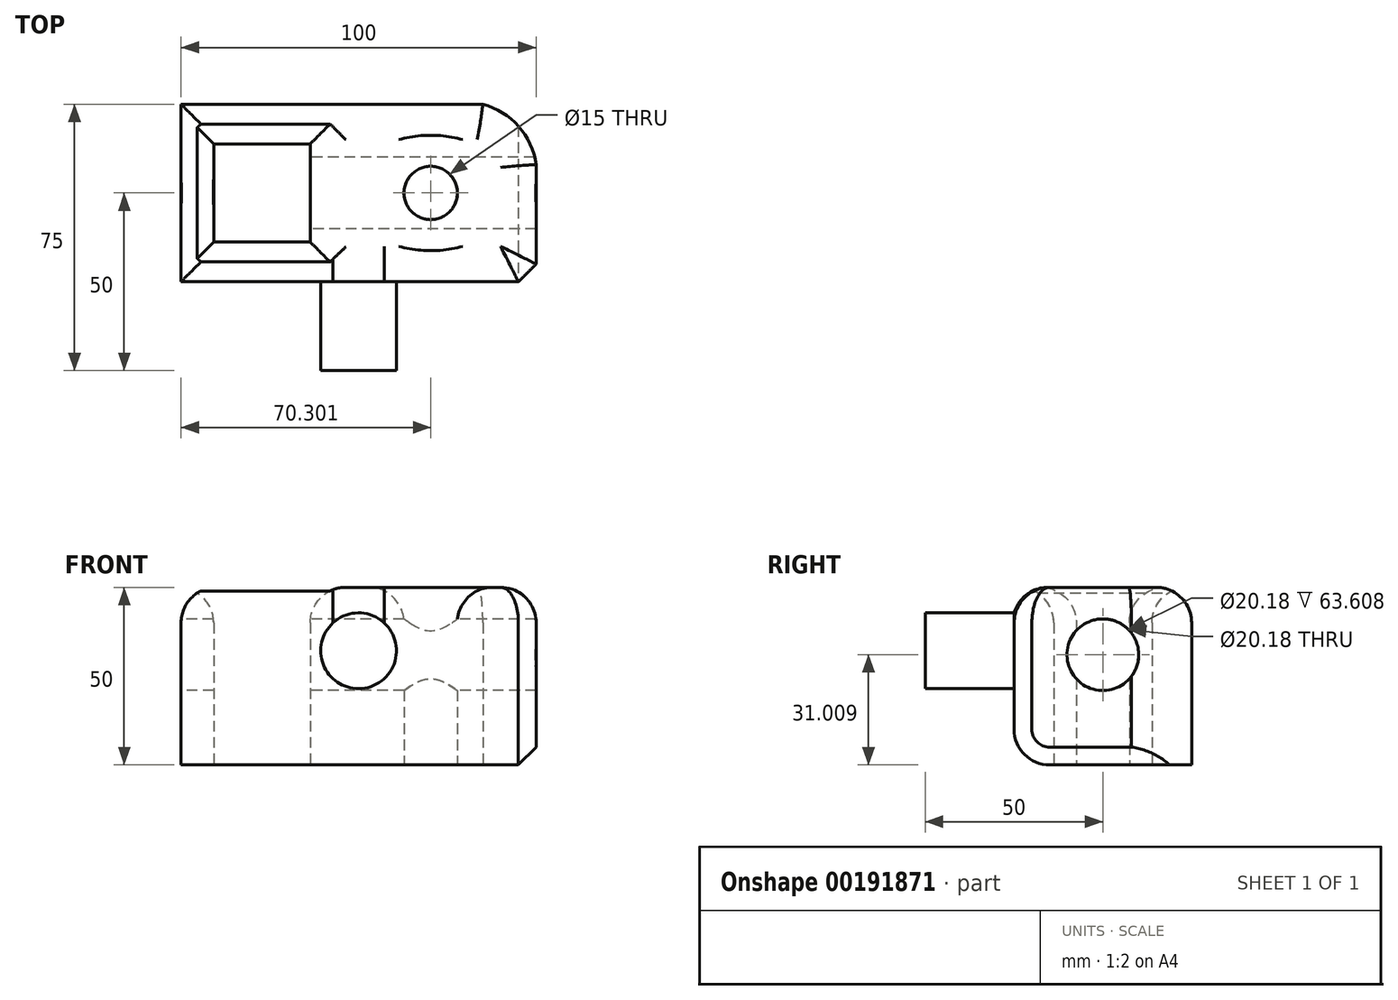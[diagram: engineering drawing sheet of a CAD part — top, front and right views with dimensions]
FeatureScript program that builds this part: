
annotation { "Feature Type Name" : "Feature", "Feature Type Description" : "" }
export const myFeature = defineFeature(function(context is Context, id is Id, definition is map)
    precondition{}
    {
        {
            var Q0;
            Q0=qCreatedBy(makeId("Top.planeOp"),FACE);
            var sketch = newSketch(context, id + "F0", { "sketchPlane" : qUnion([Q0])});
            skLineSegment(sketch, "E0.bottom", {"start": v(50, -25) * mm, "end": v(-50, -25) * mm});
            skLineSegment(sketch, "E0.top", {"start": v(35, 25) * mm, "end": v(-50, 25) * mm});
            skLineSegment(sketch, "E0.left", {"start": v(50, -25) * mm, "end": v(50, 8.03) * mm});
            skLineSegment(sketch, "E0.right", {"start": v(-50, -25) * mm, "end": v(-50, 25) * mm});
            skPoint(sketch, "E0.middle", {"position": v(0, 0) * mm});
            skLineSegment(sketch, "E1.bottom", {"start": v(-13.6, -13.83) * mm, "end": v(-40.83, -13.83) * mm});
            skLineSegment(sketch, "E1.top", {"start": v(-13.6, 13.83) * mm, "end": v(-40.83, 13.83) * mm});
            skLineSegment(sketch, "E1.left", {"start": v(-13.6, -13.83) * mm, "end": v(-13.6, 13.83) * mm});
            skLineSegment(sketch, "E1.right", {"start": v(-40.83, -13.83) * mm, "end": v(-40.83, 13.83) * mm});
            skPoint(sketch, "E1.middle", {"position": v(-27.22, 0) * mm});
            skPoint(sketch, "E1.middle.positionSnap0", {"position": v(-50, 0) * mm});
            skPoint(sketch, "E1.centerSnap0", {"position": v(-50, 0) * mm});
            skArc(sketch, "E2", {"start": v(50, 8.03) * mm, "mid": v(45.05, 18.77) * mm, "end": v(35, 25) * mm});
            skPoint(sketch, "E3.orphan", {"position": v(50, 25) * mm});
            skCircle(sketch, "E4", {"center": v(20.3, 0) * mm, "radius": 7.5 * mm});
            skSolve(sketch);
        }
        {
            var Q0;
            Q0=makeQuery(id+"F0.imprint","IMPRINT",FACE,{"disambiguationData":[TD([[makeQuery(id+"F0.imprint","IMPRINT",EDGE,{"derivedFrom":sQuery(id+"F0.wireOp",EDGE,"E0.bottom")}),-1.0]])]});
            extrude(context, id + "F1", {"entities" : qUnion([Q0]), "depth" : 50 * mm});
        }
        {
            var Q0;
            Q0=makeQuery(id+"F1.opExtrude","SWEPT_FACE",FACE,{"disambiguationData":[OSD([sQuery(id+"F0.wireOp",EDGE,"E0.bottom")])]});
            var sketch = newSketch(context, id + "F2", { "sketchPlane" : qUnion([Q0])});
            skCircle(sketch, "E5", {"center": v(0, 32.12) * mm, "radius": 10.66 * mm});
            skSolve(sketch);
        }
        {
            var Q0;
            Q0=makeQuery(id+"F2.imprint","IMPRINT",FACE,{"disambiguationData":[TD([[makeQuery(id+"F2.imprint","IMPRINT",EDGE,{"derivedFrom":sQuery(id+"F2.wireOp",EDGE,"E5")}),1.0]])]});
            extrude(context, id + "F3", {"entities" : qUnion([Q0]), "operationType" : NewBodyOperationType.ADD, "depth" : 25 * mm});
        }
        {
            var Q0;
            Q0=makeQuery(id+"F1.opExtrude","SWEPT_FACE",FACE,{"disambiguationData":[OSD([sQuery(id+"F0.wireOp",EDGE,"E0.right")])]});
            var sketch = newSketch(context, id + "F4", { "sketchPlane" : qUnion([Q0])});
            skCircle(sketch, "E6", {"center": v(0, 31) * mm, "radius": 10.09 * mm});
            skSolve(sketch);
        }
        {
            var Q0;
            Q0=makeQuery(id+"F4.imprint","IMPRINT",FACE,{"disambiguationData":[TD([[makeQuery(id+"F4.imprint","IMPRINT",EDGE,{"derivedFrom":sQuery(id+"F4.wireOp",EDGE,"E6")}),1.0]])]});
            extrude(context, id + "F5", {"entities" : qUnion([Q0]), "operationType" : NewBodyOperationType.REMOVE, "oppositeDirection" : true, "depth" : 200 * mm});
        }
        {
            var Q0;
            Q0=makeQuery(id+"F1.opExtrude","CAP_EDGE",EDGE,{"disambiguationData":[OSD([sQuery(id+"F0.wireOp",EDGE,"E0.bottom")])],"isStart":false});
            var Q1;
            Q1=makeQuery(id+"F1.opExtrude","CAP_EDGE",EDGE,{"disambiguationData":[OSD([sQuery(id+"F0.wireOp",EDGE,"E0.bottom")])],"isStart":true});
            var Q2;
            Q2=makeQuery(id+"F1.opExtrude","CAP_FACE",FACE,{"disambiguationData":[OSD([sQuery(id+"F0.wireOp",EDGE,"E0.bottom"),sQuery(id+"F0.wireOp",EDGE,"E0.top"),sQuery(id+"F0.wireOp",EDGE,"E0.left"),sQuery(id+"F0.wireOp",EDGE,"E0.right"),sQuery(id+"F0.wireOp",EDGE,"E1.bottom"),sQuery(id+"F0.wireOp",EDGE,"E1.top"),sQuery(id+"F0.wireOp",EDGE,"E1.left"),sQuery(id+"F0.wireOp",EDGE,"E1.right"),sQuery(id+"F0.wireOp",EDGE,"E2"),sQuery(id+"F0.wireOp",EDGE,"E4")])],"isStart":false});
            fillet(context, id + "F6", {"entities" : qUnion([Q0, Q1, Q2]), "radius" : 10 * mm, "tangentPropagation" : true, "allowEdgeOverflow" : false});
        }
        {
            var Q0;
            Q0=makeQuery(id+"F1.opExtrude","SWEPT_EDGE",EDGE,{"disambiguationData":[OSD([sQuery(id+"F0.wireOp",EDGE,"E0.bottom"),sQuery(id+"F0.wireOp",EDGE,"E0.left")])]});
            chamfer(context, id + "F7", {"entities" : qUnion([Q0]), "width" : 5 * mm, "tangentPropagation" : true});
        }
    });
